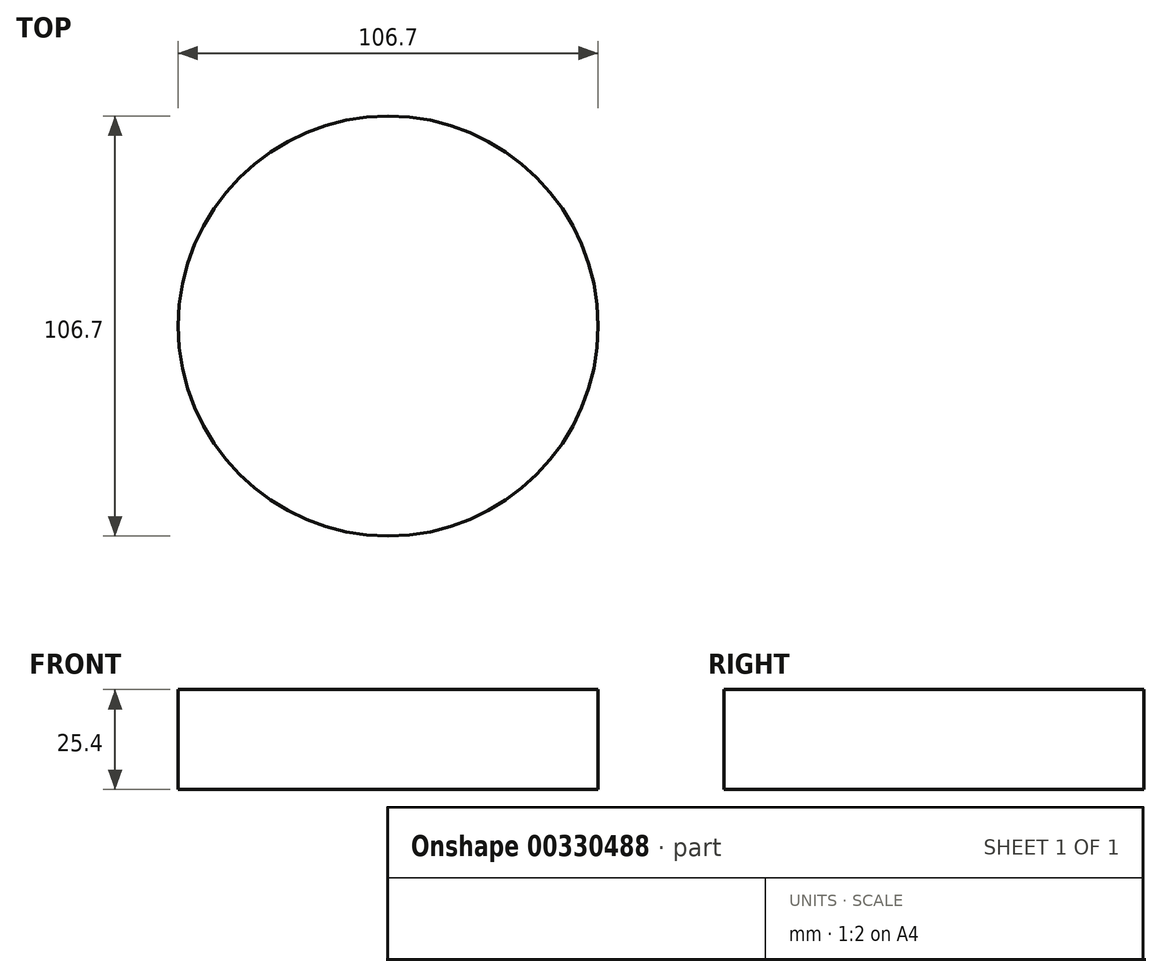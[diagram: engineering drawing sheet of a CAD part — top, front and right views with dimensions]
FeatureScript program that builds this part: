
annotation { "Feature Type Name" : "Feature", "Feature Type Description" : "" }
export const myFeature = defineFeature(function(context is Context, id is Id, definition is map)
    precondition{}
    {
        {
            var Q0;
            Q0=qCreatedBy(makeId("Top.planeOp"),FACE);
            var sketch = newSketch(context, id + "F0", { "sketchPlane" : qUnion([Q0])});
            skCircle(sketch, "E0", {"center": v(0, 0) * mm, "radius": 53.35 * mm});
            skSolve(sketch);
        }
        {
            var Q0;
            Q0 = qSketchRegion(id + "F0", true);
            extrude(context, id + "F1", {"entities" : qUnion([Q0]), "depth" : 25.4 * mm});
        }
    });
